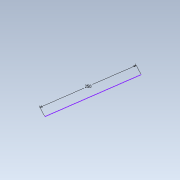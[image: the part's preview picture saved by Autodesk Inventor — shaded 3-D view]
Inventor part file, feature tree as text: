
AUTODESK INVENTOR PART (.ipt)
format: ipt  version: 2021 (Build 250183000, 183)  size: 64,512 bytes
history: native  units: mm
features: sketch x1
ambient origin geometry x8: Origin, YZ Plane, XZ Plane, XY Plane, X Axis, Y Axis, Z Axis, Center Point
feature tree (1):
  sketch  "Sketch1"  dims[d0=250.0mm]
